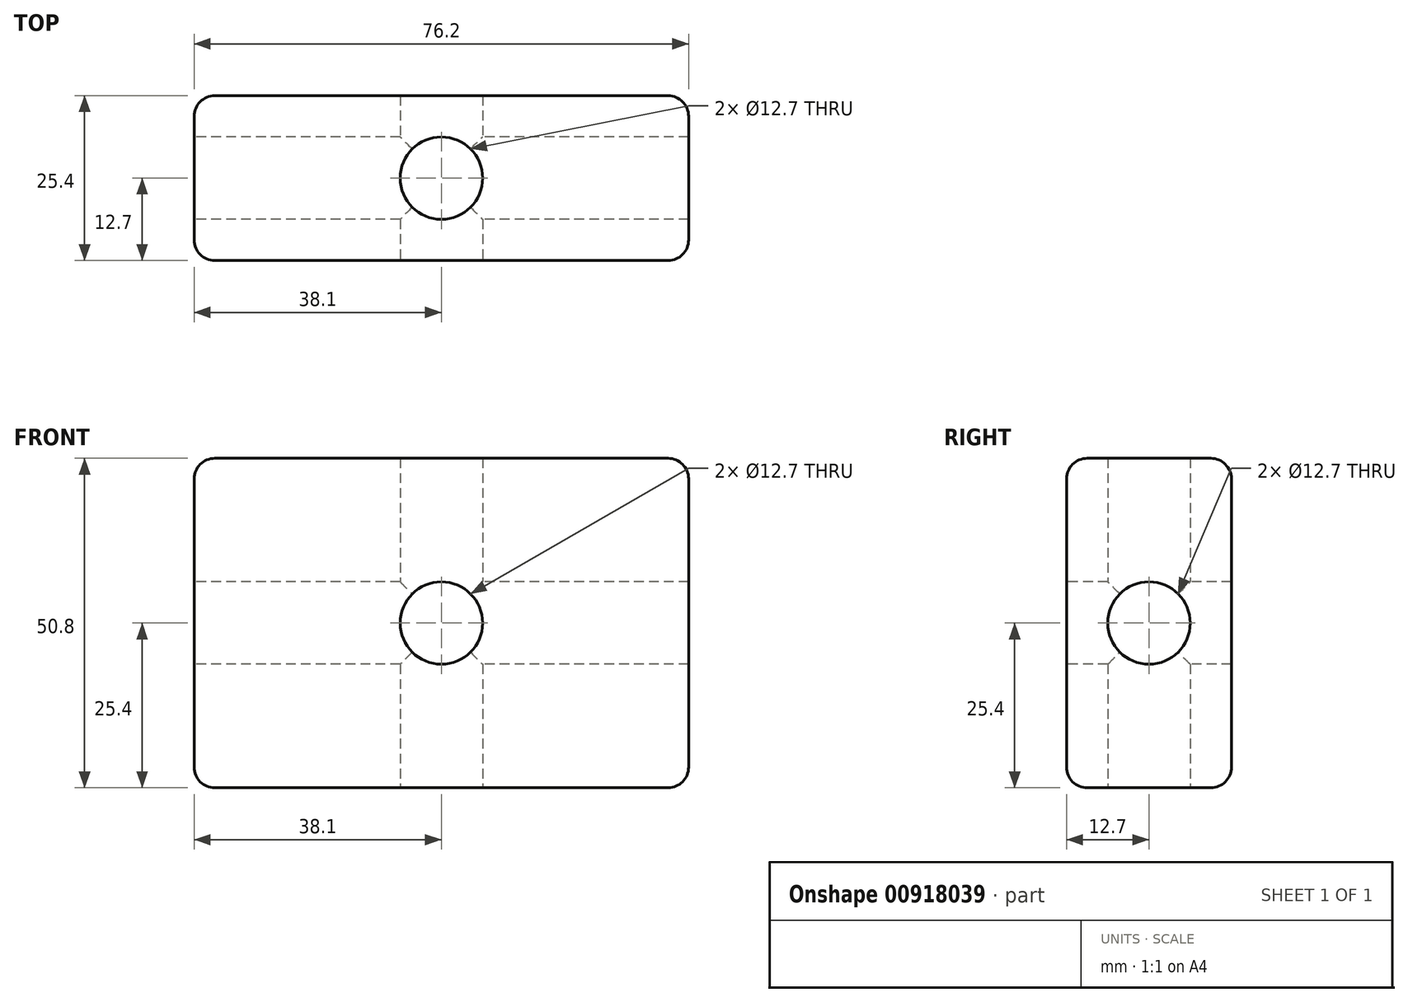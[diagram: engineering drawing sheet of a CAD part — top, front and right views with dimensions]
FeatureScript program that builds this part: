
annotation { "Feature Type Name" : "Feature", "Feature Type Description" : "" }
export const myFeature = defineFeature(function(context is Context, id is Id, definition is map)
    precondition{}
    {
        {
            var Q0;
            Q0=qCreatedBy(makeId("Front.planeOp"),FACE);
            var sketch = newSketch(context, id + "F0", { "sketchPlane" : qUnion([Q0])});
            skLineSegment(sketch, "E0.bottom", {"start": v(0, 0) * mm, "end": v(76.2, 0) * mm});
            skLineSegment(sketch, "E0.top", {"start": v(0, 50.8) * mm, "end": v(76.2, 50.8) * mm});
            skLineSegment(sketch, "E0.left", {"start": v(0, 0) * mm, "end": v(0, 50.8) * mm});
            skLineSegment(sketch, "E0.right", {"start": v(76.2, 0) * mm, "end": v(76.2, 50.8) * mm});
            skSolve(sketch);
        }
        {
            var Q0;
            Q0 = qSketchRegion(id + "F0", true);
            extrude(context, id + "F1", {"entities" : qUnion([Q0]), "depth" : 25.4 * mm, "offsetDistance" : 25.4 * mm});
        }
        {
            var Q0;
            Q0=makeQuery(id+"F1.opExtrude","CAP_FACE",FACE,{"disambiguationData":[OSD([sQuery(id+"F0.wireOp",EDGE,"E0.bottom"),sQuery(id+"F0.wireOp",EDGE,"E0.top"),sQuery(id+"F0.wireOp",EDGE,"E0.left"),sQuery(id+"F0.wireOp",EDGE,"E0.right")])],"isStart":false});
            var sketch = newSketch(context, id + "F2", { "sketchPlane" : qUnion([Q0])});
            skCircle(sketch, "E1", {"center": v(38.1, 25.4) * mm, "radius": 6.35 * mm});
            skSolve(sketch);
        }
        {
            var Q0;
            Q0 = qSketchRegion(id + "F2", true);
            extrude(context, id + "F3", {"entities" : qUnion([Q0]), "operationType" : NewBodyOperationType.REMOVE, "endBound" : BoundingType.THROUGH_ALL, "oppositeDirection" : true, "depth" : 25.4 * mm, "offsetDistance" : 25.4 * mm});
        }
        {
            var Q0;
            Q0=makeQuery(id+"F1.opExtrude","SWEPT_FACE",FACE,{"disambiguationData":[OSD([sQuery(id+"F0.wireOp",EDGE,"E0.left")])]});
            var sketch = newSketch(context, id + "F4", { "sketchPlane" : qUnion([Q0])});
            skCircle(sketch, "E2", {"center": v(12.7, 25.4) * mm, "radius": 6.35 * mm});
            skSolve(sketch);
        }
        {
            var Q0;
            Q0 = qSketchRegion(id + "F4", true);
            extrude(context, id + "F5", {"entities" : qUnion([Q0]), "operationType" : NewBodyOperationType.REMOVE, "endBound" : BoundingType.THROUGH_ALL, "oppositeDirection" : true, "depth" : 25.4 * mm, "offsetDistance" : 25.4 * mm});
        }
        {
            var Q0;
            Q0=makeQuery(id+"F1.opExtrude","SWEPT_FACE",FACE,{"disambiguationData":[OSD([sQuery(id+"F0.wireOp",EDGE,"E0.bottom")])]});
            var sketch = newSketch(context, id + "F6", { "sketchPlane" : qUnion([Q0])});
            skCircle(sketch, "E3", {"center": v(38.1, 12.7) * mm, "radius": 6.35 * mm});
            skSolve(sketch);
        }
        {
            var Q0;
            Q0 = qSketchRegion(id + "F6", true);
            extrude(context, id + "F7", {"entities" : qUnion([Q0]), "operationType" : NewBodyOperationType.REMOVE, "endBound" : BoundingType.THROUGH_ALL, "oppositeDirection" : true, "depth" : 25.4 * mm, "offsetDistance" : 25.4 * mm});
        }
        {
            var Q0;
            Q0=makeQuery(id+"F1.opExtrude","SWEPT_EDGE",EDGE,{"disambiguationData":[OSD([sQuery(id+"F0.wireOp",EDGE,"E0.top"),sQuery(id+"F0.wireOp",EDGE,"E0.left")])]});
            var Q1;
            Q1=makeQuery(id+"F1.opExtrude","CAP_EDGE",EDGE,{"disambiguationData":[OSD([sQuery(id+"F0.wireOp",EDGE,"E0.left")])],"isStart":false});
            var Q2;
            Q2=makeQuery(id+"F1.opExtrude","CAP_EDGE",EDGE,{"disambiguationData":[OSD([sQuery(id+"F0.wireOp",EDGE,"E0.bottom")])],"isStart":false});
            var Q3;
            Q3=makeQuery(id+"F1.opExtrude","CAP_EDGE",EDGE,{"disambiguationData":[OSD([sQuery(id+"F0.wireOp",EDGE,"E0.right")])],"isStart":false});
            var Q4;
            Q4=makeQuery(id+"F1.opExtrude","SWEPT_EDGE",EDGE,{"disambiguationData":[OSD([sQuery(id+"F0.wireOp",EDGE,"E0.top"),sQuery(id+"F0.wireOp",EDGE,"E0.right")])]});
            var Q5;
            Q5=makeQuery(id+"F1.opExtrude","CAP_EDGE",EDGE,{"disambiguationData":[OSD([sQuery(id+"F0.wireOp",EDGE,"E0.right")])],"isStart":true});
            var Q6;
            Q6=makeQuery(id+"F1.opExtrude","CAP_EDGE",EDGE,{"disambiguationData":[OSD([sQuery(id+"F0.wireOp",EDGE,"E0.top")])],"isStart":false});
            var Q7;
            Q7=makeQuery(id+"F1.opExtrude","CAP_EDGE",EDGE,{"disambiguationData":[OSD([sQuery(id+"F0.wireOp",EDGE,"E0.top")])],"isStart":true});
            var Q8;
            Q8=makeQuery(id+"F1.opExtrude","CAP_EDGE",EDGE,{"disambiguationData":[OSD([sQuery(id+"F0.wireOp",EDGE,"E0.bottom")])],"isStart":true});
            var Q9;
            Q9=makeQuery(id+"F1.opExtrude","SWEPT_EDGE",EDGE,{"disambiguationData":[OSD([sQuery(id+"F0.wireOp",EDGE,"E0.bottom"),sQuery(id+"F0.wireOp",EDGE,"E0.left")])]});
            var Q10;
            Q10=makeQuery(id+"F1.opExtrude","CAP_EDGE",EDGE,{"disambiguationData":[OSD([sQuery(id+"F0.wireOp",EDGE,"E0.left")])],"isStart":true});
            var Q11;
            Q11=makeQuery(id+"F1.opExtrude","SWEPT_EDGE",EDGE,{"disambiguationData":[OSD([sQuery(id+"F0.wireOp",EDGE,"E0.bottom"),sQuery(id+"F0.wireOp",EDGE,"E0.right")])]});
            fillet(context, id + "F8", {"entities" : qUnion([Q0, Q1, Q2, Q3, Q4, Q5, Q6, Q7, Q8, Q9, Q10, Q11]), "radius" : 3.17 * mm, "tangentPropagation" : true, "allowEdgeOverflow" : false});
        }
    });
